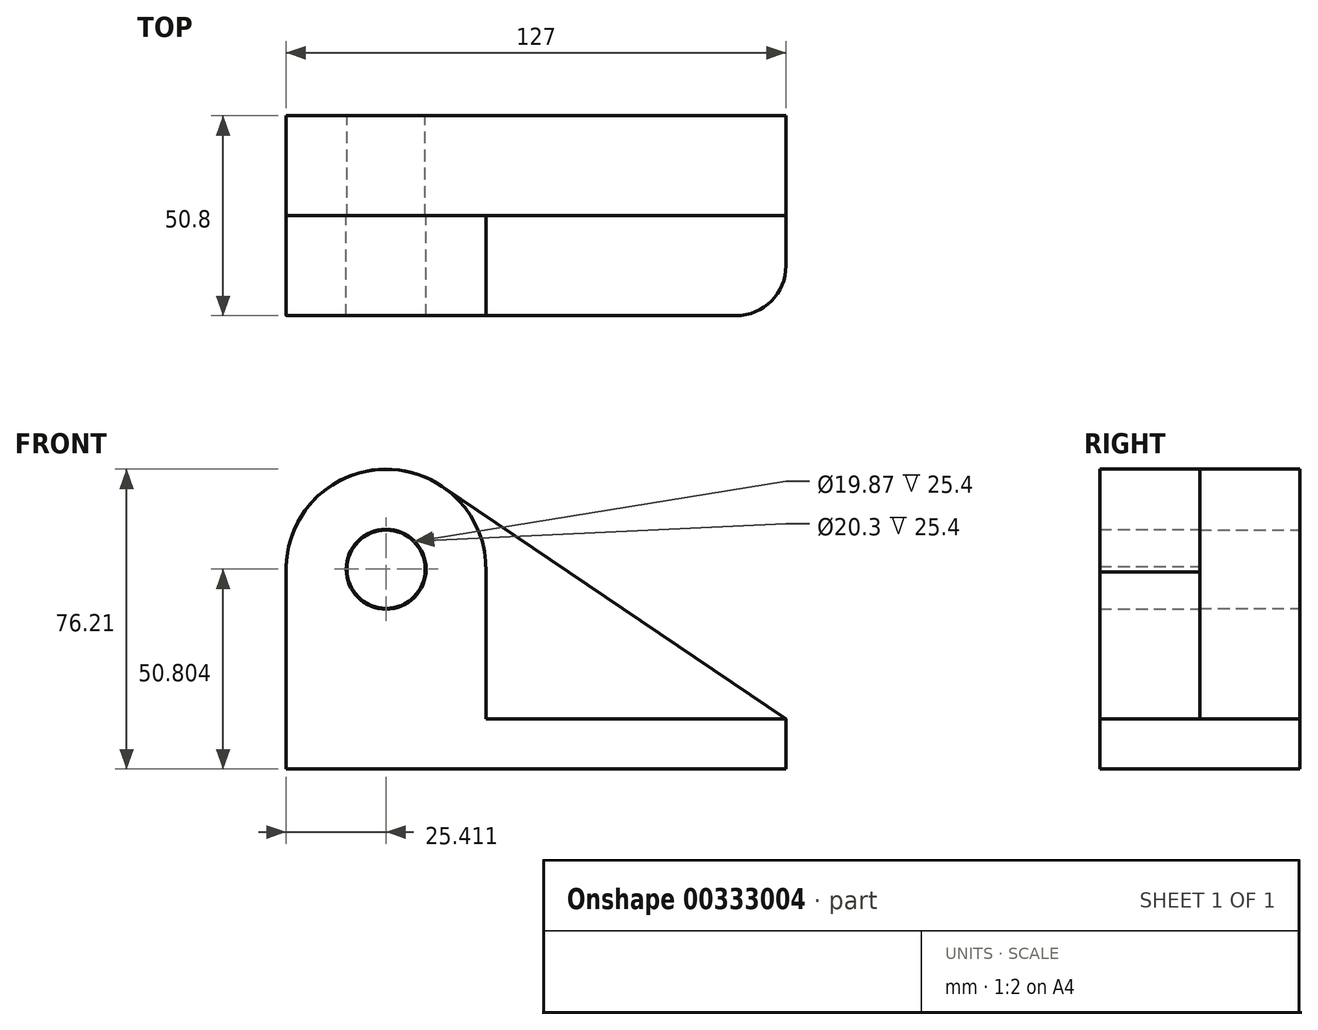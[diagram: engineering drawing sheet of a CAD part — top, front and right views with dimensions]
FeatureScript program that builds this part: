
annotation { "Feature Type Name" : "Feature", "Feature Type Description" : "" }
export const myFeature = defineFeature(function(context is Context, id is Id, definition is map)
    precondition{}
    {
        {
            var Q0;
            Q0=qCreatedBy(makeId("Front.planeOp"),FACE);
            var sketch = newSketch(context, id + "F0", { "sketchPlane" : qUnion([Q0])});
            skArc(sketch, "E0", {"start": v(-53.16, 63.96) * mm, "mid": v(-79.3, 65.37) * mm, "end": v(-92.8, 42.92) * mm});
            skCircle(sketch, "E1", {"center": v(-67.4, 42.92) * mm, "radius": 9.93 * mm});
            skLineSegment(sketch, "E2", {"start": v(-92.8, 42.92) * mm, "end": v(-92.8, -7.88) * mm});
            skLineSegment(sketch, "E3", {"start": v(-92.8, -7.88) * mm, "end": v(34.2, -7.88) * mm});
            skLineSegment(sketch, "E4", {"start": v(34.2, -7.88) * mm, "end": v(34.2, 4.82) * mm});
            skLineSegment(sketch, "E5", {"start": v(34.2, 4.82) * mm, "end": v(-53.16, 63.96) * mm});
            skSolve(sketch);
        }
        {
            var Q0;
            Q0 = qSketchRegion(id + "F0", true);
            extrude(context, id + "F1", {"entities" : qUnion([Q0]), "depth" : 25.4 * mm});
        }
        {
            var Q0;
            Q0=makeQuery(id+"F1.opExtrude","CAP_FACE",FACE,{"disambiguationData":[OSD([sQuery(id+"F0.wireOp",EDGE,"E0"),sQuery(id+"F0.wireOp",EDGE,"E1"),sQuery(id+"F0.wireOp",EDGE,"E2"),sQuery(id+"F0.wireOp",EDGE,"E3"),sQuery(id+"F0.wireOp",EDGE,"E4"),sQuery(id+"F0.wireOp",EDGE,"E5")])],"isStart":false});
            var sketch = newSketch(context, id + "F2", { "sketchPlane" : qUnion([Q0])});
            skArc(sketch, "E6", {"start": v(-42, 42.27) * mm, "mid": v(-66.75, 68.32) * mm, "end": v(-92.8, 43.58) * mm});
            skCircle(sketch, "E7", {"center": v(-67.4, 42.92) * mm, "radius": 10.15 * mm});
            skLineSegment(sketch, "E8.bottom", {"start": v(34.2, 4.82) * mm, "end": v(-42, 4.82) * mm});
            skLineSegment(sketch, "E8.top", {"start": v(34.2, -7.88) * mm, "end": v(-92.8, -7.88) * mm});
            skLineSegment(sketch, "E8.left", {"start": v(34.2, 4.82) * mm, "end": v(34.2, -7.88) * mm});
            skLineSegment(sketch, "E8.right", {"start": v(-92.8, 4.82) * mm, "end": v(-92.8, -7.88) * mm});
            skLineSegment(sketch, "E9", {"start": v(-92.8, 43.58) * mm, "end": v(-92.8, 43.58) * mm});
            skLineSegment(sketch, "E10", {"start": v(-42, 42.27) * mm, "end": v(-42, 4.82) * mm});
            skPoint(sketch, "E11.orphan", {"position": v(-42, 0) * mm});
            skSolve(sketch);
        }
        {
            var Q0;
            Q0=makeQuery(id+"F2.imprint","IMPRINT",FACE,{"disambiguationData":[TD([[makeQuery(id+"F2.imprint","IMPRINT",EDGE,{"derivedFrom":sQuery(id+"F2.wireOp",EDGE,"E6")}),1.0]])]});
            extrude(context, id + "F3", {"entities" : qUnion([Q0]), "operationType" : NewBodyOperationType.ADD, "depth" : 25.4 * mm});
        }
        {
            var Q0;
            Q0=makeQuery(id+"F3.opExtrude","CAP_EDGE",EDGE,{"disambiguationData":[OSD([sQuery(id+"F2.wireOp",EDGE,"E8.left")])],"isStart":false});
            fillet(context, id + "F4", {"entities" : qUnion([Q0]), "radius" : 12.7 * mm, "tangentPropagation" : true, "allowEdgeOverflow" : false});
        }
    });
